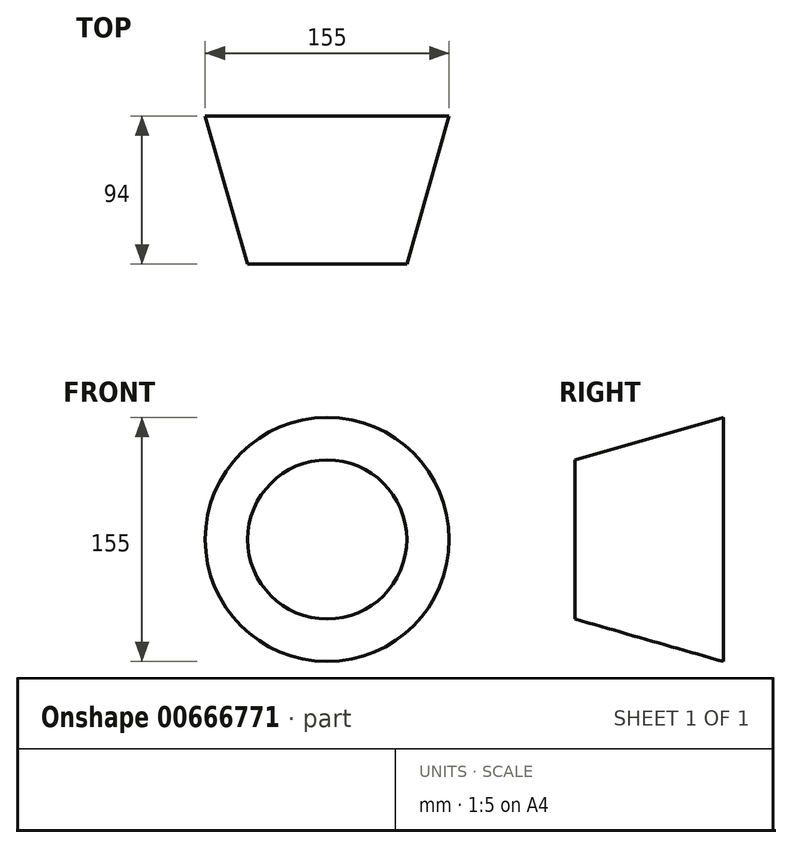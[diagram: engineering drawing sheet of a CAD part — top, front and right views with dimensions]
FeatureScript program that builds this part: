
annotation { "Feature Type Name" : "Feature", "Feature Type Description" : "" }
export const myFeature = defineFeature(function(context is Context, id is Id, definition is map)
    precondition{}
    {
        {
            var Q0;
            Q0=qCreatedBy(makeId("Front.planeOp"),FACE);
            var sketch = newSketch(context, id + "F0", { "sketchPlane" : qUnion([Q0])});
            skCircle(sketch, "E0", {"center": v(0, 0) * mm, "radius": 77.5 * mm});
            skSolve(sketch);
        }
        {
            var Q0;
            Q0 = qSketchRegion(id + "F0", true);
            extrude(context, id + "F1", {"entities" : qUnion([Q0]), "depth" : 94 * mm, "offsetDistance" : 25 * mm, "hasDraft" : true, "draftAngle" : 16 * degree, "draftPullDirection" : true});
        }
    });
